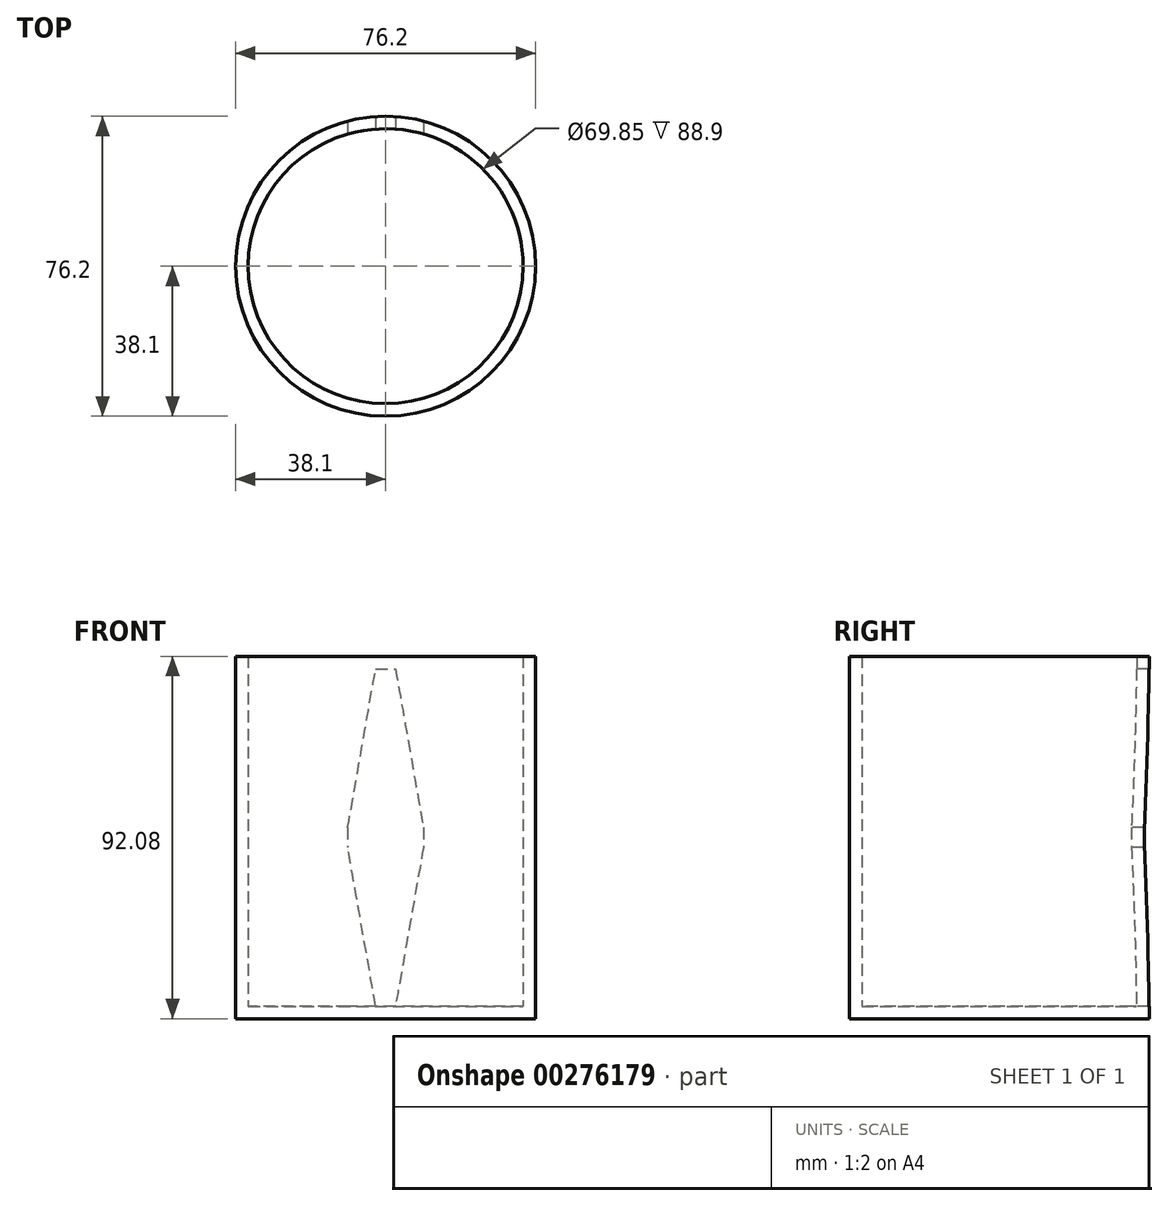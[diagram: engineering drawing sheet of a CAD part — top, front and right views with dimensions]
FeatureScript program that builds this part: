
annotation { "Feature Type Name" : "Feature", "Feature Type Description" : "" }
export const myFeature = defineFeature(function(context is Context, id is Id, definition is map)
    precondition{}
    {
        {
            var Q0;
            Q0=qCreatedBy(makeId("Top.planeOp"),FACE);
            var sketch = newSketch(context, id + "F0", { "sketchPlane" : qUnion([Q0])});
            skCircle(sketch, "E0", {"center": v(0, 0) * mm, "radius": 38.1 * mm});
            skSolve(sketch);
        }
        {
            var Q0;
            Q0=qSketchRegion(id+"F0",true);
            extrude(context, id + "F1", {"entities" : qUnion([Q0]), "depth" : 3.17 * mm});
        }
        {
            var Q0;
            Q0=makeQuery(id+"F1.opExtrude","CAP_FACE",FACE,{"disambiguationData":[OSD([sQuery(id+"F0.wireOp",EDGE,"E0")])],"isStart":false});
            var sketch = newSketch(context, id + "F2", { "sketchPlane" : qUnion([Q0])});
            skCircle(sketch, "E1.0", {"center": v(0, 0) * mm, "radius": 38.1 * mm});
            skCircle(sketch, "E2.0", {"center": v(0, 0) * mm, "radius": 34.93 * mm});
            skSolve(sketch);
        }
        {
            var Q0;
            Q0=qSketchRegion(id+"F2",true);
            extrude(context, id + "F3", {"entities" : qUnion([Q0]), "operationType" : NewBodyOperationType.ADD, "depth" : 88.9 * mm});
        }
        {
            var Q0;
            Q0=qCreatedBy(makeId("Front.planeOp"),FACE);
            var sketch = newSketch(context, id + "F4", { "sketchPlane" : qUnion([Q0])});
            skLineSegment(sketch, "E3", {"start": v(-2.5, 88.9) * mm, "end": v(2.5, 88.9) * mm});
            skLineSegment(sketch, "E4", {"start": v(2.5, 88.9) * mm, "end": v(9.62, 48.54) * mm});
            skLineSegment(sketch, "E5", {"start": v(9.62, 48.54) * mm, "end": v(9.62, 43.54) * mm});
            skLineSegment(sketch, "E6", {"start": v(9.62, 43.54) * mm, "end": v(2.5, 3.17) * mm});
            skLineSegment(sketch, "E7", {"start": v(2.5, 3.18) * mm, "end": v(-2.5, 3.18) * mm});
            skLineSegment(sketch, "E8", {"start": v(-2.5, 3.17) * mm, "end": v(-9.62, 43.54) * mm});
            skLineSegment(sketch, "E9", {"start": v(-9.62, 43.54) * mm, "end": v(-9.62, 48.54) * mm});
            skLineSegment(sketch, "E10", {"start": v(-9.62, 48.54) * mm, "end": v(-2.5, 88.9) * mm});
            skLineSegment(sketch, "E11", {"start": v(-2.5, 88.9) * mm, "end": v(2.5, 3.18) * mm, "construction": true});
            skLineSegment(sketch, "E12", {"start": v(0, 0) * mm, "end": v(0, 92.12) * mm, "construction": true});
            skPoint(sketch, "E13", {"position": v(0, 46.04) * mm});
            skSolve(sketch);
        }
        {
            var Q0;
            Q0=qSketchRegion(id+"F4",true);
            extrude(context, id + "F5", {"entities" : qUnion([Q0]), "operationType" : NewBodyOperationType.REMOVE, "endBound" : BoundingType.THROUGH_ALL, "oppositeDirection" : true, "depth" : 25 * mm});
        }
        {
            var Q0;
            Q0=qCreatedBy(makeId("Right.planeOp"),FACE);
            var sketch = newSketch(context, id + "F6", { "sketchPlane" : qUnion([Q0])});
            skLineSegment(sketch, "E14", {"start": v(0, 0) * mm, "end": v(0, 120.33) * mm});
            skSolve(sketch);
        }
    });
